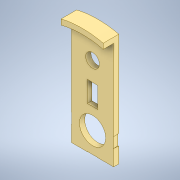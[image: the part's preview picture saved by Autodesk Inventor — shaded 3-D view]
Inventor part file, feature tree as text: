
AUTODESK INVENTOR PART (.ipt)
format: ipt  version: 2020.1 (Build 241239000, 239)  size: 264,192 bytes
history: native  units: in
note: dims shown in document units (in); Inventor stores cm internally (conversion verified against a paired STEP export)
features: sketch x5, extrude x3, plane x3, split x3, hole x2, pattern_circular x2, projected_geometry x2, other x1, fillet x1
ambient origin geometry x8: Origin, YZ Plane, XZ Plane, XY Plane, X Axis, Y Axis, Z Axis, Center Point
bodies: Solid1 (feature_tree)
feature tree (22):
  parser-record x1  (decoder bookkeeping rows leaked as tree rows — omitted from the tree; the rows remain in map.json)
  extrude  "Extrusion1"  Depth=0.0787in
  extrude  "Extrusion2"  Depth=0.0787in
  hole  "Hole1"  [1 undecoded]
  hole  "Hole2"  [1 undecoded]
  pattern_circular  "Circular Pattern1"  [2 undecoded]
  extrude  "Extrusion5"  Depth=0.3181in
  fillet  "Fillet2"  [1 undecoded]
  pattern_circular  "Circular Pattern3"  [2 undecoded]
  plane  "Work Plane1"
  plane  "Work Plane2"
  plane  "Work Plane3"
  split  "Split1"
  split  "Split2"
  split  "Split3"
  sketch  "Sketch1"  dims[d0=2.8346in d1=0.0787in]
  sketch  "Sketch2"  dims[d2=0.0in d3=0.0787in]
  projected_geometry  "Projected Loop1"
  sketch  "Sketch4"  dims[d4=0.1575in d5=0.0in]
  sketch  "Sketch5"  dims[d6=0.3976in]
  sketch  "Sketch8"  dims[d7=0.75in d8=0.375in d9=0.25in d10=0.5635in d11=1.0in d12=0.8108in d13=0.9186in d14=0.2087in d15=0.75in d16=0.375in d17=0.25in d18=0.5635in d19=1.0in d20=0.8108in d21=1.9685in d22=360.0deg d43=0.1575in d44=0.315in d45=0.315in d46=1.0in d47=0.0137in d48=0.0787in d52=0.0098in d53=1.5748in d54=360.0deg d56=0.3181in d57=-0.3181in d58=-0.3181in d23=0.0625in d24=0.75in d25=0.375in]
  projected_geometry  "Projected Loop2"
note: 7 required parameter values undecoded (feature->parameter linkage not recoverable at this tier; creation-order binding heuristic only, values carry confidence <= 0.55)
note: 1 file-system path scrubbed to <path> (originals preserved in map.json)
